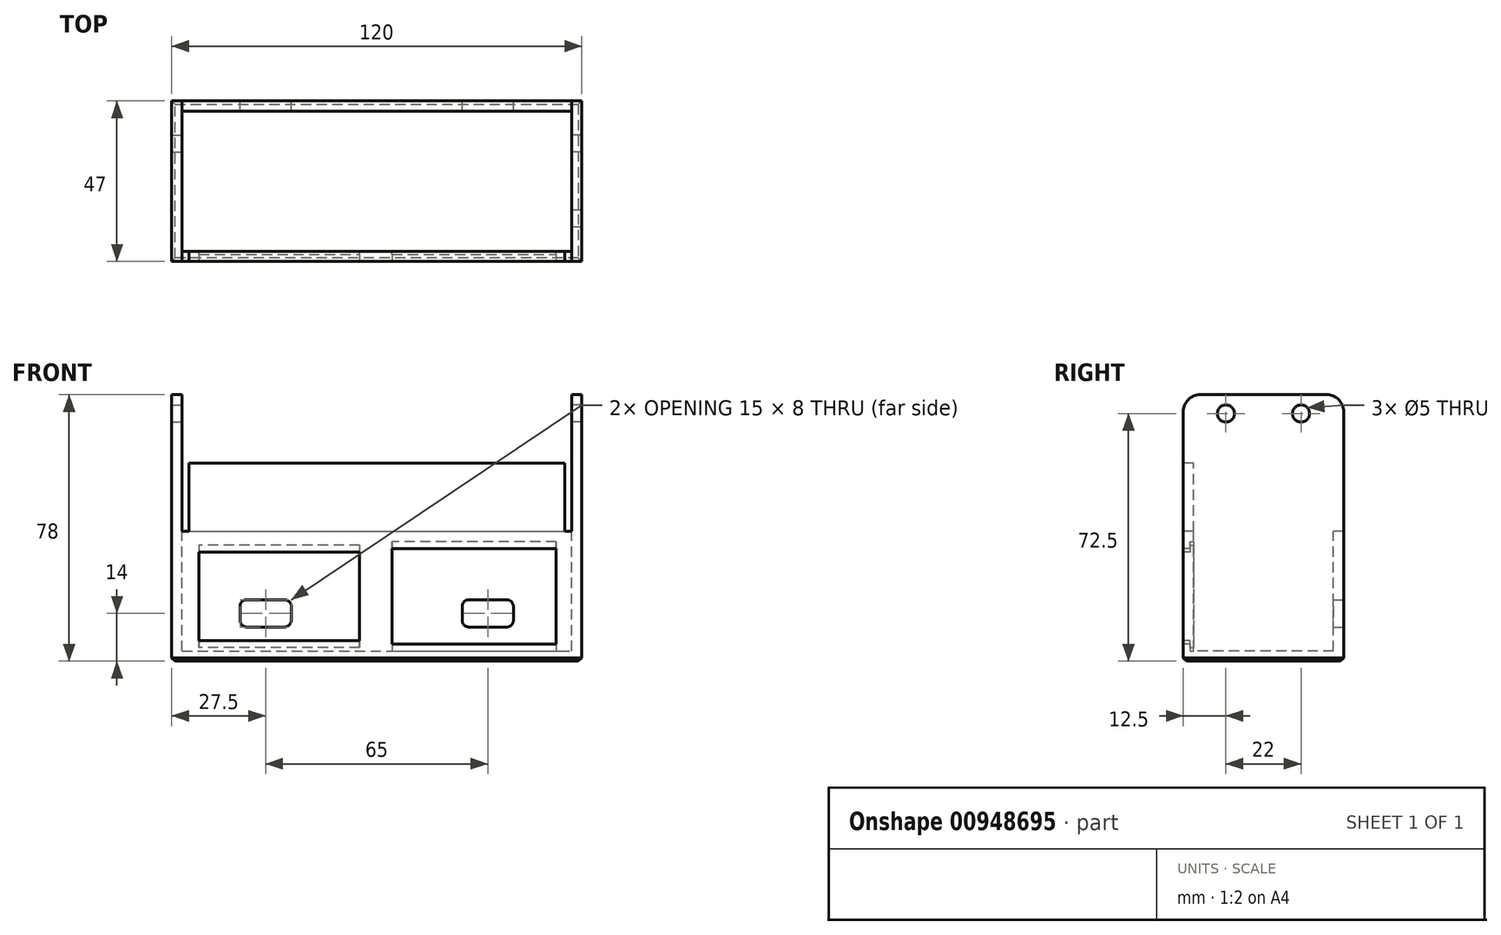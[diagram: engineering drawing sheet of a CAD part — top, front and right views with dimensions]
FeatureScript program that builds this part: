
annotation { "Feature Type Name" : "Feature", "Feature Type Description" : "" }
export const myFeature = defineFeature(function(context is Context, id is Id, definition is map)
    precondition{}
    {
        {
            assignVariable(context, id + "F0", {"name" : "wall", "anyValue" : 3});
        }
        {
            assignVariable(context, id + "F1", {"name" : "width", "anyValue" : 114});
        }
        {
            var Q0;
            Q0=qCreatedBy(makeId("Right.planeOp"),FACE);
            var sketch = newSketch(context, id + "F2", { "sketchPlane" : qUnion([Q0])});
            skLineSegment(sketch, "E0.bottom", {"start": v(17.5, 40) * mm, "end": v(-19.5, 40) * mm});
            skLineSegment(sketch, "E0.top", {"start": v(22.5, -38) * mm, "end": v(-24.5, -38) * mm});
            skLineSegment(sketch, "E0.left", {"start": v(22.5, 35) * mm, "end": v(22.5, -38) * mm});
            skLineSegment(sketch, "E0.right", {"start": v(-24.5, 35) * mm, "end": v(-24.5, -38) * mm});
            skCircle(sketch, "E1", {"center": v(10, 34.5) * mm, "radius": 2.5 * mm});
            skCircle(sketch, "E2", {"center": v(-12, 34.5) * mm, "radius": 2.5 * mm});
            skPoint(sketch, "E3.visualSharp", {"position": v(-24.5, 40) * mm});
            skArc(sketch, "E3.filletArc", {"start": v(-19.5, 40) * mm, "mid": v(-23.04, 38.54) * mm, "end": v(-24.5, 35) * mm});
            skPoint(sketch, "E4.visualSharp", {"position": v(22.5, 40) * mm});
            skArc(sketch, "E4.filletArc", {"start": v(22.5, 35) * mm, "mid": v(21.04, 38.54) * mm, "end": v(17.5, 40) * mm});
            skSolve(sketch);
        }
        {
            var Q0;
            Q0=qSketchRegion(id+"F2",true);
            extrude(context, id + "F3", {"entities" : qUnion([Q0]), "depth" : (getVariable(context, 'wall')) * mm, "offsetDistance" : 25 * mm});
        }
        {
            var Q0;
            Q0=qCreatedBy(makeId("Right.planeOp"),FACE);
            var sketch = newSketch(context, id + "F4", { "sketchPlane" : qUnion([Q0])});
            skLineSegment(sketch, "E5.bottom", {"start": v(22.5, -38) * mm, "end": v(-24.5, -38) * mm});
            skLineSegment(sketch, "E5.top", {"start": v(22.5, -35) * mm, "end": v(-24.5, -35) * mm});
            skLineSegment(sketch, "E5.left", {"start": v(22.5, -38) * mm, "end": v(22.5, -35) * mm});
            skLineSegment(sketch, "E5.right", {"start": v(-24.5, -38) * mm, "end": v(-24.5, -35) * mm});
            skLineSegment(sketch, "E6.bottom", {"start": v(-24.5, -38) * mm, "end": v(-21.5, -38) * mm});
            skLineSegment(sketch, "E6.top", {"start": v(-24.5, 0) * mm, "end": v(-21.5, 0) * mm});
            skLineSegment(sketch, "E6.left", {"start": v(-24.5, -38) * mm, "end": v(-24.5, 0) * mm});
            skLineSegment(sketch, "E6.right", {"start": v(-21.5, -38) * mm, "end": v(-21.5, 0) * mm});
            skLineSegment(sketch, "E7.bottom", {"start": v(22.5, -38) * mm, "end": v(19.5, -38) * mm});
            skLineSegment(sketch, "E7.top", {"start": v(22.5, 0) * mm, "end": v(19.5, 0) * mm});
            skLineSegment(sketch, "E7.left", {"start": v(22.5, -38) * mm, "end": v(22.5, 0) * mm});
            skLineSegment(sketch, "E7.right", {"start": v(19.5, -38) * mm, "end": v(19.5, 0) * mm});
            skSolve(sketch);
        }
        {
            var Q0;
            {var subQ0=sQuery(id+"F4.wireOp",EDGE,"E5.right");var subQ1=sQuery(id+"F4.wireOp",EDGE,"E5.bottom");var subQ9=sQuery(id+"F4.wireOp",EDGE,"E7.right");var subQ10=makeQuery(id+"F4.imprint","INTERSECT",VERTEX,{"derivedFrom":[subQ1,subQ9]});var subQ14=sQuery(id+"F4.wireOp",EDGE,"E5.left");var subQ16=sQuery(id+"F4.wireOp",EDGE,"E7.top");var subQ17=sQuery(id+"F4.wireOp",EDGE,"E6.top");Q0=qUnion([makeQuery(id+"F4.imprint","IMPRINT",FACE,{"disambiguationData":[TD([[makeQuery(id+"F4.imprint","IMPRINT",EDGE,{"derivedFrom":subQ17}),-1.0]])]}),makeQuery(id+"F4.imprint","IMPRINT",FACE,{"disambiguationData":[TD([[makeQuery(id+"F4.imprint","IMPRINT",EDGE,{"derivedFrom":subQ14}),1.0]])]}),makeQuery(id+"F4.imprint","IMPRINT",FACE,{"disambiguationData":[TD([[makeQuery(id+"F4.imprint","IMPRINT",EDGE,{"derivedFrom":subQ16}),1.0]])]}),makeQuery(id+"F4.imprint","IMPRINT",FACE,{"disambiguationData":[TD([[makeQuery(id+"F4.imprint","IMPRINT",EDGE,{"disambiguationData":[TD([[subQ10,-1.0]])],"derivedFrom":subQ1}),-1.0]])]}),makeQuery(id+"F4.imprint","IMPRINT",FACE,{"disambiguationData":[TD([[makeQuery(id+"F4.imprint","IMPRINT",EDGE,{"derivedFrom":subQ0}),-1.0]])]})]);}
            extrude(context, id + "F5", {"entities" : qUnion([Q0]), "operationType" : NewBodyOperationType.ADD, "oppositeDirection" : true, "depth" : (getVariable(context, 'width')) * mm, "offsetDistance" : 25 * mm});
        }
        {
            var Q0;
            Q0=makeQuery(id+"F5.opExtrude","CAP_FACE",FACE,{"disambiguationData":[OSD([sQuery(id+"F4.wireOp",EDGE,"E5.bottom"),sQuery(id+"F4.wireOp",EDGE,"E5.top"),sQuery(id+"F4.wireOp",EDGE,"E5.left"),sQuery(id+"F4.wireOp",EDGE,"E5.right"),sQuery(id+"F4.wireOp",EDGE,"E6.top"),sQuery(id+"F4.wireOp",EDGE,"E6.left"),sQuery(id+"F4.wireOp",EDGE,"E6.right"),sQuery(id+"F4.wireOp",EDGE,"E7.top"),sQuery(id+"F4.wireOp",EDGE,"E7.left"),sQuery(id+"F4.wireOp",EDGE,"E7.right")])],"isStart":false});
            var sketch = newSketch(context, id + "F6", { "sketchPlane" : qUnion([Q0])});
            skLineSegment(sketch, "E8.bottom", {"start": v(19.5, 40) * mm, "end": v(-17.5, 40) * mm});
            skLineSegment(sketch, "E8.top", {"start": v(24.5, -38) * mm, "end": v(-22.5, -38) * mm});
            skLineSegment(sketch, "E8.left", {"start": v(24.5, 35) * mm, "end": v(24.5, -38) * mm});
            skLineSegment(sketch, "E8.right", {"start": v(-22.5, 35) * mm, "end": v(-22.5, -38) * mm});
            skCircle(sketch, "E9", {"center": v(-10, 34.5) * mm, "radius": 2.5 * mm});
            skPoint(sketch, "E10.visualSharp", {"position": v(-22.5, 40) * mm});
            skArc(sketch, "E10.filletArc", {"start": v(-17.5, 40) * mm, "mid": v(-21.04, 38.54) * mm, "end": v(-22.5, 35) * mm});
            skPoint(sketch, "E11.visualSharp", {"position": v(24.5, 40) * mm});
            skArc(sketch, "E11.filletArc", {"start": v(24.5, 35) * mm, "mid": v(23.04, 38.54) * mm, "end": v(19.5, 40) * mm});
            skSolve(sketch);
        }
        {
            var Q0;
            Q0=qSketchRegion(id+"F6",true);
            extrude(context, id + "F7", {"entities" : qUnion([Q0]), "operationType" : NewBodyOperationType.ADD, "depth" : (getVariable(context, 'wall')) * mm, "offsetDistance" : 25 * mm});
        }
        {
            var Q0;
            Q0=makeQuery(id+"F7.boolean.opBoolean","MERGE",FACE,{"derivedFrom":[makeQuery(id+"F5.boolean.opBoolean","MERGE",FACE,{"derivedFrom":[makeQuery(id+"F3.opExtrude","SWEPT_FACE",FACE,{"disambiguationData":[OSD([sQuery(id+"F2.wireOp",EDGE,"E0.right")])]}),makeQuery(id+"F5.opExtrude","SWEPT_FACE",FACE,{"disambiguationData":[OSD([sQuery(id+"F4.wireOp",EDGE,"E5.right"),sQuery(id+"F4.wireOp",EDGE,"E6.left")])]})]}),makeQuery(id+"F7.opExtrude","SWEPT_FACE",FACE,{"disambiguationData":[OSD([sQuery(id+"F6.wireOp",EDGE,"E8.left")])]})]});
            var sketch = newSketch(context, id + "F8", { "sketchPlane" : qUnion([Q0])});
            skLineSegment(sketch, "E12.bottom", {"start": v(-112, 0) * mm, "end": v(-2, 0) * mm});
            skLineSegment(sketch, "E12.top", {"start": v(-112, 20) * mm, "end": v(-2, 20) * mm});
            skLineSegment(sketch, "E12.left", {"start": v(-112, 0) * mm, "end": v(-112, 20) * mm});
            skLineSegment(sketch, "E12.right", {"start": v(-2, 0) * mm, "end": v(-2, 20) * mm});
            skSolve(sketch);
        }
        {
            var Q0;
            Q0=qSketchRegion(id+"F8",true);
            extrude(context, id + "F9", {"entities" : qUnion([Q0]), "operationType" : NewBodyOperationType.ADD, "oppositeDirection" : true, "depth" : (getVariable(context, 'wall')) * mm, "offsetDistance" : 25 * mm});
        }
        {
            var Q0;
            {var subQ2=sQuery(id+"F8.wireOp",EDGE,"E12.bottom");Q0=makeQuery(id+"F8.imprint","IMPRINT",FACE,{"disambiguationData":[TD([[makeQuery(id+"F8.imprint","IMPRINT",EDGE,{"derivedFrom":subQ2}),-1.0]])]});}
            var sketch = newSketch(context, id + "F10", { "sketchPlane" : qUnion([Q0])});
            skLineSegment(sketch, "E13.bottom", {"start": v(-109, -6) * mm, "end": v(-62, -6) * mm});
            skLineSegment(sketch, "E13.top", {"start": v(-109, -32) * mm, "end": v(-62, -32) * mm});
            skLineSegment(sketch, "E13.left", {"start": v(-109, -6) * mm, "end": v(-109, -32) * mm});
            skLineSegment(sketch, "E13.right", {"start": v(-62, -6) * mm, "end": v(-62, -32) * mm});
            skLineSegment(sketch, "E14.bottom", {"start": v(-52.5, -5) * mm, "end": v(-4.5, -5) * mm});
            skLineSegment(sketch, "E14.top", {"start": v(-52.5, -33) * mm, "end": v(-4.5, -33) * mm});
            skLineSegment(sketch, "E14.left", {"start": v(-52.5, -5) * mm, "end": v(-52.5, -33) * mm});
            skLineSegment(sketch, "E14.right", {"start": v(-4.5, -5) * mm, "end": v(-4.5, -33) * mm});
            skLineSegment(sketch, "E15", {"start": v(-57, 0) * mm, "end": v(-57, -48.8) * mm, "construction": true});
            skLineSegment(sketch, "E16", {"start": v(-121.46, -19) * mm, "end": v(11.47, -19) * mm, "construction": true});
            skSolve(sketch);
        }
        {
            var Q0;
            Q0=qSketchRegion(id+"F10",true);
            extrude(context, id + "F11", {"entities" : qUnion([Q0]), "operationType" : NewBodyOperationType.REMOVE, "endBound" : BoundingType.UP_TO_NEXT, "oppositeDirection" : true, "depth" : 25 * mm, "offsetDistance" : 25 * mm});
        }
        {
            var Q0;
            Q0=makeQuery(id+"F7.boolean.opBoolean","MERGE",FACE,{"derivedFrom":[makeQuery(id+"F5.boolean.opBoolean","MERGE",FACE,{"derivedFrom":[makeQuery(id+"F3.opExtrude","SWEPT_FACE",FACE,{"disambiguationData":[OSD([sQuery(id+"F2.wireOp",EDGE,"E0.left")])]}),makeQuery(id+"F5.opExtrude","SWEPT_FACE",FACE,{"disambiguationData":[OSD([sQuery(id+"F4.wireOp",EDGE,"E5.left"),sQuery(id+"F4.wireOp",EDGE,"E7.left")])]})]}),makeQuery(id+"F7.opExtrude","SWEPT_FACE",FACE,{"disambiguationData":[OSD([sQuery(id+"F6.wireOp",EDGE,"E8.right")])]})]});
            var sketch = newSketch(context, id + "F12", { "sketchPlane" : qUnion([Q0])});
            skLineSegment(sketch, "E17.bottom", {"start": v(84, -28) * mm, "end": v(95, -28) * mm});
            skLineSegment(sketch, "E17.top", {"start": v(84, -20) * mm, "end": v(95, -20) * mm});
            skLineSegment(sketch, "E17.left", {"start": v(82, -26) * mm, "end": v(82, -22) * mm});
            skLineSegment(sketch, "E17.right", {"start": v(97, -26) * mm, "end": v(97, -22) * mm});
            skPoint(sketch, "E18.visualSharp", {"position": v(82, -28) * mm});
            skArc(sketch, "E18.filletArc", {"start": v(82, -26) * mm, "mid": v(82.59, -27.41) * mm, "end": v(84, -28) * mm});
            skPoint(sketch, "E19.visualSharp", {"position": v(82, -20) * mm});
            skArc(sketch, "E19.filletArc", {"start": v(84, -20) * mm, "mid": v(82.59, -20.59) * mm, "end": v(82, -22) * mm});
            skPoint(sketch, "E20.visualSharp", {"position": v(97, -20) * mm});
            skArc(sketch, "E20.filletArc", {"start": v(97, -22) * mm, "mid": v(96.41, -20.59) * mm, "end": v(95, -20) * mm});
            skPoint(sketch, "E21.visualSharp", {"position": v(97, -28) * mm});
            skArc(sketch, "E21.filletArc", {"start": v(95, -28) * mm, "mid": v(96.41, -27.41) * mm, "end": v(97, -26) * mm});
            skArc(sketch, "E22.MirrorCS", {"start": v(19, -28) * mm, "mid": v(17.59, -27.41) * mm, "end": v(17, -26) * mm});
            skArc(sketch, "E23.MirrorCS", {"start": v(17, -22) * mm, "mid": v(17.59, -20.59) * mm, "end": v(19, -20) * mm});
            skArc(sketch, "E24.MirrorCS", {"start": v(30, -20) * mm, "mid": v(31.41, -20.59) * mm, "end": v(32, -22) * mm});
            skArc(sketch, "E25.MirrorCS", {"start": v(32, -26) * mm, "mid": v(31.41, -27.41) * mm, "end": v(30, -28) * mm});
            skLineSegment(sketch, "E26.MirrorCS", {"start": v(17, -26) * mm, "end": v(17, -22) * mm});
            skLineSegment(sketch, "E27.MirrorCS", {"start": v(32, -26) * mm, "end": v(32, -22) * mm});
            skPoint(sketch, "E28.MirrorP", {"position": v(17, -20) * mm});
            skPoint(sketch, "E29.MirrorP", {"position": v(32, -20) * mm});
            skPoint(sketch, "E30.MirrorP", {"position": v(32, -28) * mm});
            skLineSegment(sketch, "E31.MirrorCS", {"start": v(30, -28) * mm, "end": v(19, -28) * mm});
            skLineSegment(sketch, "E32.MirrorCS", {"start": v(30, -20) * mm, "end": v(19, -20) * mm});
            skPoint(sketch, "E33.MirrorP", {"position": v(17, -28) * mm});
            skSolve(sketch);
        }
        {
            var Q0;
            Q0=qSketchRegion(id+"F12",true);
            extrude(context, id + "F13", {"entities" : qUnion([Q0]), "operationType" : NewBodyOperationType.REMOVE, "endBound" : BoundingType.UP_TO_NEXT, "oppositeDirection" : true, "depth" : 25 * mm, "offsetDistance" : 25 * mm});
        }
        {
            var Q0;
            Q0=makeQuery(id+"F7.boolean.opBoolean","MERGE",FACE,{"derivedFrom":[makeQuery(id+"F5.boolean.opBoolean","MERGE",FACE,{"derivedFrom":[makeQuery(id+"F3.opExtrude","SWEPT_FACE",FACE,{"disambiguationData":[OSD([sQuery(id+"F2.wireOp",EDGE,"E0.top")])]}),makeQuery(id+"F5.opExtrude","SWEPT_FACE",FACE,{"disambiguationData":[OSD([sQuery(id+"F4.wireOp",EDGE,"E5.bottom")])]})]}),makeQuery(id+"F7.opExtrude","SWEPT_FACE",FACE,{"disambiguationData":[OSD([sQuery(id+"F6.wireOp",EDGE,"E8.top")])]})]});
            chamfer(context, id + "F14", {"entities" : qUnion([Q0]), "width" : 1 * mm, "tangentPropagation" : true});
        }
        {
            assignVariable(context, id + "F15", {"name" : "InsertClipD", "anyValue" : 1});
        }
        {
            var Q0;
            Q0=makeQuery(id+"F9.boolean.opBoolean","MERGE",FACE,{"derivedFrom":[makeQuery(id+"F5.opExtrude","SWEPT_FACE",FACE,{"disambiguationData":[OSD([sQuery(id+"F4.wireOp",EDGE,"E6.right")])]}),makeQuery(id+"F9.opExtrude","CAP_FACE",FACE,{"disambiguationData":[OSD([sQuery(id+"F8.wireOp",EDGE,"E12.bottom"),sQuery(id+"F8.wireOp",EDGE,"E12.top"),sQuery(id+"F8.wireOp",EDGE,"E12.left"),sQuery(id+"F8.wireOp",EDGE,"E12.right")])],"isStart":false})]});
            var sketch = newSketch(context, id + "F16", { "sketchPlane" : qUnion([Q0])});
            skLineSegment(sketch, "E34.bottom", {"start": v(4.5, -5) * mm, "end": v(52.5, -5) * mm});
            skLineSegment(sketch, "E34.top", {"start": v(4.5, -3) * mm, "end": v(52.5, -3) * mm});
            skLineSegment(sketch, "E34.left", {"start": v(4.5, -5) * mm, "end": v(4.5, -3) * mm});
            skLineSegment(sketch, "E34.right", {"start": v(52.5, -5) * mm, "end": v(52.5, -3) * mm});
            skLineSegment(sketch, "E35.bottom", {"start": v(4.5, -33) * mm, "end": v(52.5, -33) * mm});
            skLineSegment(sketch, "E35.top", {"start": v(4.5, -35) * mm, "end": v(52.5, -35) * mm});
            skLineSegment(sketch, "E35.left", {"start": v(4.5, -33) * mm, "end": v(4.5, -35) * mm});
            skLineSegment(sketch, "E35.right", {"start": v(52.5, -33) * mm, "end": v(52.5, -35) * mm});
            skLineSegment(sketch, "E36.bottom", {"start": v(62, -4) * mm, "end": v(109, -4) * mm});
            skLineSegment(sketch, "E36.top", {"start": v(62, -6) * mm, "end": v(109, -6) * mm});
            skLineSegment(sketch, "E36.left", {"start": v(62, -4) * mm, "end": v(62, -6) * mm});
            skLineSegment(sketch, "E36.right", {"start": v(109, -4) * mm, "end": v(109, -6) * mm});
            skLineSegment(sketch, "E37.bottom", {"start": v(62, -34) * mm, "end": v(109, -34) * mm});
            skLineSegment(sketch, "E37.top", {"start": v(62, -32) * mm, "end": v(109, -32) * mm});
            skLineSegment(sketch, "E37.left", {"start": v(62, -34) * mm, "end": v(62, -32) * mm});
            skLineSegment(sketch, "E37.right", {"start": v(109, -34) * mm, "end": v(109, -32) * mm});
            skSolve(sketch);
        }
        {
            var Q0;
            Q0=makeQuery(id+"F16.imprint","IMPRINT",FACE,{"disambiguationData":[TD([[makeQuery(id+"F16.imprint","IMPRINT",EDGE,{"derivedFrom":sQuery(id+"F16.wireOp",EDGE,"E35.bottom")}),1.0]])]});
            var Q1;
            Q1=makeQuery(id+"F16.imprint","IMPRINT",FACE,{"disambiguationData":[TD([[makeQuery(id+"F16.imprint","IMPRINT",EDGE,{"derivedFrom":sQuery(id+"F16.wireOp",EDGE,"E37.bottom")}),1.0]])]});
            var Q2;
            Q2=makeQuery(id+"F16.imprint","IMPRINT",FACE,{"disambiguationData":[TD([[makeQuery(id+"F16.imprint","IMPRINT",EDGE,{"derivedFrom":sQuery(id+"F16.wireOp",EDGE,"E36.bottom")}),-1.0]])]});
            var Q3;
            Q3=makeQuery(id+"F16.imprint","IMPRINT",FACE,{"disambiguationData":[TD([[makeQuery(id+"F16.imprint","IMPRINT",EDGE,{"derivedFrom":sQuery(id+"F16.wireOp",EDGE,"E34.bottom")}),-1.0]])]});
            extrude(context, id + "F17", {"entities" : qUnion([Q0, Q1, Q2, Q3]), "operationType" : NewBodyOperationType.REMOVE, "oppositeDirection" : true, "depth" : (getVariable(context, 'InsertClipD')) * mm, "offsetDistance" : 25 * mm});
        }
    });
